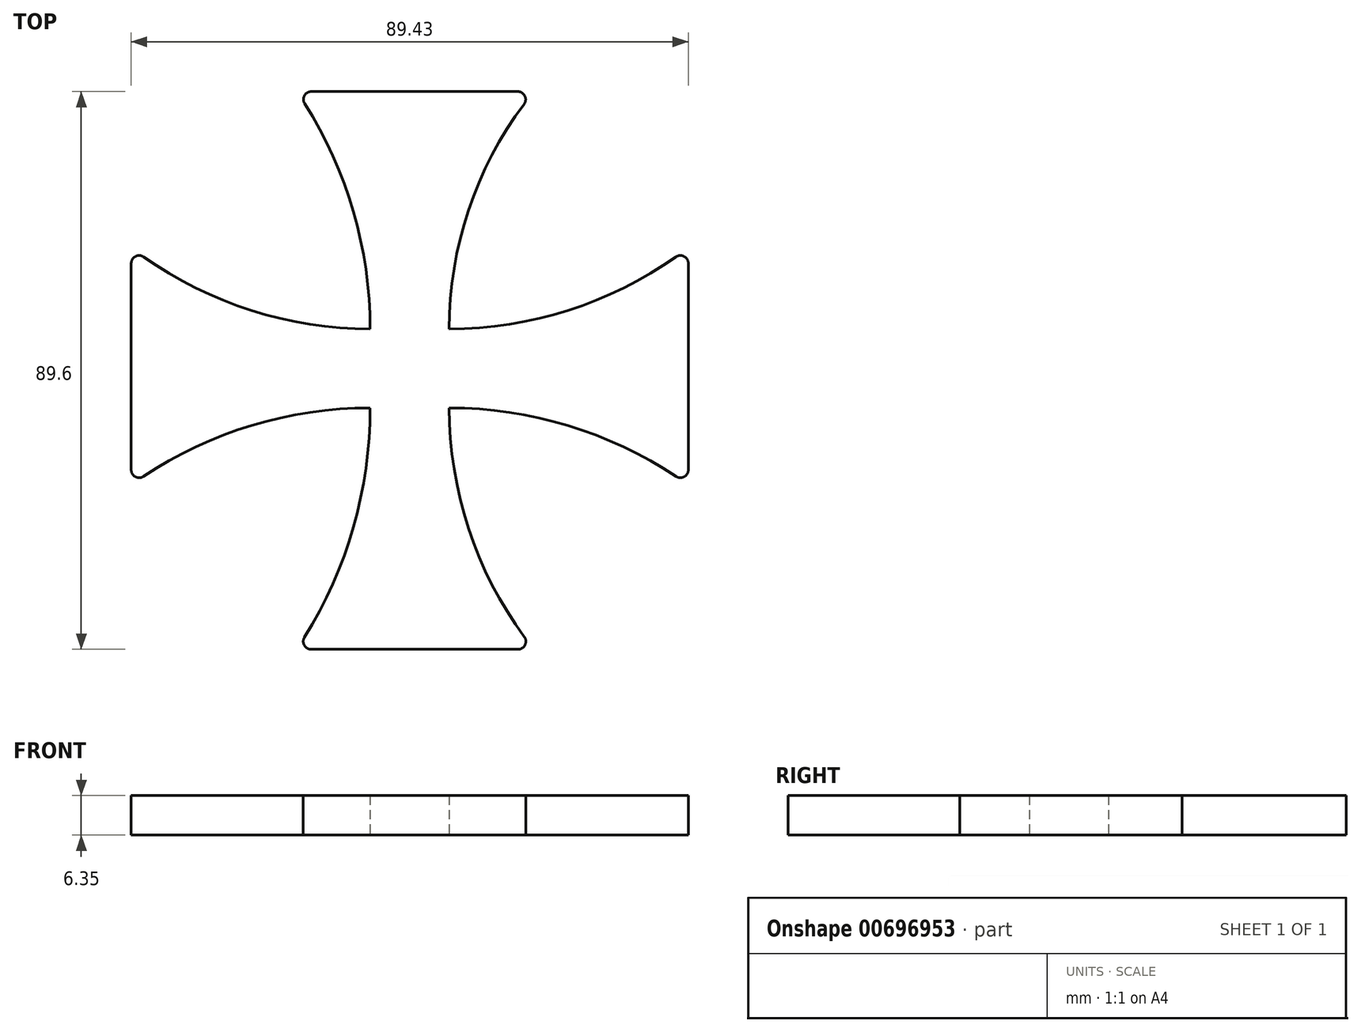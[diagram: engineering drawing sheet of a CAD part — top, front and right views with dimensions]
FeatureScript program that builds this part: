
annotation { "Feature Type Name" : "Feature", "Feature Type Description" : "" }
export const myFeature = defineFeature(function(context is Context, id is Id, definition is map)
    precondition{}
    {
        {
            var Q0;
            Q0=qCreatedBy(makeId("Top.planeOp"),FACE);
            var sketch = newSketch(context, id + "F0", { "sketchPlane" : qUnion([Q0])});
            skLineSegment(sketch, "E0.bottom", {"start": v(-3.84, 8.04) * mm, "end": v(8.86, 8.04) * mm});
            skLineSegment(sketch, "E0.top", {"start": v(-3.84, -4.66) * mm, "end": v(8.86, -4.66) * mm});
            skLineSegment(sketch, "E0.left", {"start": v(-3.84, 8.04) * mm, "end": v(-3.84, -4.66) * mm});
            skLineSegment(sketch, "E0.right", {"start": v(8.86, 8.04) * mm, "end": v(8.86, -4.66) * mm});
            skLineSegment(sketch, "E1", {"start": v(-13.27, 46.17) * mm, "end": v(19.86, 46.17) * mm});
            skLineSegment(sketch, "E2", {"start": v(-42.19, 18.57) * mm, "end": v(-42.19, -14.6) * mm});
            skLineSegment(sketch, "E3", {"start": v(-13.3, -43.43) * mm, "end": v(19.9, -43.43) * mm});
            skLineSegment(sketch, "E4", {"start": v(47.24, 18.57) * mm, "end": v(47.24, -14.6) * mm});
            skArc(sketch, "E5", {"start": v(-3.84, 8.04) * mm, "mid": v(-6.52, 26.88) * mm, "end": v(-14.34, 44.22) * mm});
            skArc(sketch, "E6", {"start": v(20.88, 44.14) * mm, "mid": v(11.95, 27.07) * mm, "end": v(8.86, 8.04) * mm});
            skArc(sketch, "E7", {"start": v(8.86, 8.04) * mm, "mid": v(27.95, 11) * mm, "end": v(45.24, 19.6) * mm});
            skArc(sketch, "E8", {"start": v(45.27, -15.65) * mm, "mid": v(27.88, -7.47) * mm, "end": v(8.86, -4.66) * mm});
            skArc(sketch, "E9", {"start": v(-3.84, -4.66) * mm, "mid": v(-22.84, -7.47) * mm, "end": v(-40.22, -15.65) * mm});
            skArc(sketch, "E10", {"start": v(-14.37, -41.5) * mm, "mid": v(-6.52, -23.81) * mm, "end": v(-3.84, -4.66) * mm});
            skArc(sketch, "E11", {"start": v(8.86, -4.66) * mm, "mid": v(11.96, -24) * mm, "end": v(20.92, -41.41) * mm});
            skArc(sketch, "E12", {"start": v(-40.19, 19.6) * mm, "mid": v(-22.9, 11) * mm, "end": v(-3.84, 8.04) * mm});
            skPoint(sketch, "E13.visualSharp", {"position": v(-42.19, 21.08) * mm});
            skArc(sketch, "E13.filletArc", {"start": v(-40.19, 19.6) * mm, "mid": v(-41.5, 19.7) * mm, "end": v(-42.19, 18.57) * mm});
            skPoint(sketch, "E14.visualSharp", {"position": v(-42.19, -17.02) * mm});
            skArc(sketch, "E14.filletArc", {"start": v(-42.19, -14.6) * mm, "mid": v(-41.52, -15.71) * mm, "end": v(-40.22, -15.65) * mm});
            skPoint(sketch, "E15.visualSharp", {"position": v(-15.63, -43.43) * mm});
            skArc(sketch, "E15.filletArc", {"start": v(-14.37, -41.5) * mm, "mid": v(-14.4, -42.78) * mm, "end": v(-13.3, -43.43) * mm});
            skPoint(sketch, "E16.visualSharp", {"position": v(22.47, -43.43) * mm});
            skArc(sketch, "E16.filletArc", {"start": v(19.9, -43.43) * mm, "mid": v(21.03, -42.74) * mm, "end": v(20.92, -41.41) * mm});
            skPoint(sketch, "E17.visualSharp", {"position": v(47.24, -17.02) * mm});
            skArc(sketch, "E17.filletArc", {"start": v(45.27, -15.65) * mm, "mid": v(46.57, -15.72) * mm, "end": v(47.24, -14.6) * mm});
            skPoint(sketch, "E18.visualSharp", {"position": v(47.24, 21.08) * mm});
            skArc(sketch, "E18.filletArc", {"start": v(47.24, 18.57) * mm, "mid": v(46.56, 19.7) * mm, "end": v(45.24, 19.6) * mm});
            skPoint(sketch, "E19.visualSharp", {"position": v(22.47, 46.17) * mm});
            skArc(sketch, "E19.filletArc", {"start": v(20.88, 44.14) * mm, "mid": v(21, 45.47) * mm, "end": v(19.86, 46.17) * mm});
            skPoint(sketch, "E20.visualSharp", {"position": v(-15.63, 46.17) * mm});
            skArc(sketch, "E20.filletArc", {"start": v(-13.27, 46.17) * mm, "mid": v(-14.38, 45.51) * mm, "end": v(-14.34, 44.22) * mm});
            skSolve(sketch);
        }
        {
            var Q0;
            Q0 = qSketchRegion(id + "F0", true);
            extrude(context, id + "F1", {"entities" : qUnion([Q0]), "depth" : 6.35 * mm, "offsetDistance" : 25.4 * mm});
        }
    });
